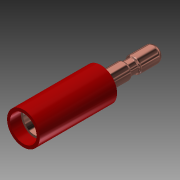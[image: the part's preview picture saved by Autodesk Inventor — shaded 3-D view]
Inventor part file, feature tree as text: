
AUTODESK INVENTOR PART (.ipt)
format: ipt  version: 2014 (Build 180170000, 170)  size: 176,128 bytes
history: native  units: in
note: dims shown in document units (in); Inventor stores cm internally (conversion verified against a paired STEP export)
features: sketch x4, projected_geometry x4, extrude x3, fillet x3, shell x1, revolve x1
ambient origin geometry x8: Origin, YZ Plane, XZ Plane, XY Plane, X Axis, Y Axis, Z Axis, Center Point
bodies: Solid1 (feature_tree), Solid2 (feature_tree)
feature tree (16):
  extrude  "Extrusion1"  Depth=0.4445in TaperAngle=0.0deg
  shell  "Shell1"  Thickness=0.0175in
  revolve  "Revolution1"  [1 undecoded]
  fillet  "Fillet1"  Radius=0.141in
  extrude  "Extrusion2"  TaperAngle=90.0deg  [1 undecoded]
  fillet  "Fillet2"  Radius=0.03in
  fillet  "Fillet3"  Radius=0.4445in
  extrude  "Extrusion3"  Depth=0.004in
  sketch  "Sketch1"  dims[d0=0.1875in d1=0.4445in d2=0.0in d3=0.0175in]
  sketch  "Sketch2"  dims[d4=0.321in d5=0.091in d6=0.141in d7=0.1375in]
  sketch  "Sketch3"  dims[d8=0.0715in d9=90.0deg d10=0.03in d11=0.4445in d12=0.0in]
  sketch  "Sketch5"  dims[d13=0.0455in d14=0.004in d15=0.015in d17=0.013in d18=0.382in d19=0.0in]
  projected_geometry  "Projected Loop2"
  projected_geometry  "Project Cut Edges1"
  projected_geometry  "Project Cut Edges2"
  projected_geometry  "Project Cut Edges3"
note: 2 required parameter values undecoded (feature->parameter linkage not recoverable at this tier; creation-order binding heuristic only, values carry confidence <= 0.55)